# Revit family: Kessel 882505DN150 en
name_source: partatom
category: Pipe Accessories
revit_build: Autodesk Revit Architecture 2014 (Build: 20130308_1515(x64)
units: mm (PartAtom-declared; Revit-internal decimal feet)

## types (1)
- Kessel 882505DN150 en
    <1.010.00.2> Number of the part of the guideline = 38
    <1.010.00.3> Issue date (month) of the guideline = 201805
    <1.010.00.4> Manufacturer name = Kessel
    <1.010.00.5> Revision date of the file = 20190228
    <1.800.00.3> BS number = 100013000000000000000000000003000000???00000000008???00000
    <1.800.00.4> Comment field = Backwater chamber CO 1000 inlet DN 150, outlet DN 150, 2680 mm
    <1.810.00.3> Manufacturer’s reference number = 882505-DN150
    <1.810.00.4> DATANORM number = 882505-DN150
    <1.810.00.6> GTIN number = 4026092071304
    <1.960/3L.00.8> Link (URL) = http://www.kessel.de
    <38.100.00.4> Drain type for floor, roof and sanitary objects = Backwater valves
    <38.110.00.4> Floor, roof and sanitary works sequences = Backwater chamber CO 1000
    <38.400.00.3> Material of the drain body = polymer
    <38.700.00.15> Connection to GLT, GA = no
    <38.700.00.16> Fire resistance class can be retrofitted = no
    <38.700.00.4> product name = Backwater chamber CO 1000 inlet DN 150, outlet DN 150, 2680 mm
    <38.700.00.6> Complete article (one-piece) from combination (multi-part design) Drain body and attachment piece = yes
    <38.700.00.7> Potential compensation (ground connection) available = no
    <38.700.00.8> Electrical connection = no
    <38.710.13.3> Product name = Backwater chamber CO 1000 inlet DN 150, outlet DN 150, 2680 mm
    <38.710.13.4> Variant of the drainage drain = point drain
    <38.710.13.7> Leafy / Kiefang = no
    <38.710.15.3> Product name = Temporary protective cover
    <38.710.15.5> Material of the drain grate = plastic
    <38.710.15.9> Slip resistance of the drain grate = no
    <38.710.16.3> Type of measurements = external dimensions
    <38.710.16.7> Mass (net) = 130.5
    CONNECTOR0_DIAMETER_dX_0r = 0 mm  [stored 0 ft]
    CONNECTOR0_dX_00 = 515 mm
    CONNECTOR0_dX_01 = 505 mm
    CONNECTOR0_ref_dX = 505 mm
    CONNECTOR1_DIAMETER_dNBN0_0r = 0 mm  [stored 0 ft]
    CONNECTOR1_dNBN0_00 = 602 mm
    CONNECTOR1_dNBN0_01 = 592 mm
    CONNECTOR1_ref_dNBN0 = 592 mm
    CONNECTOR1_ref_dNBN1 = 228 mm
    CONNECTOR2_DIAMETER_dNBN0_0r = 0 mm  [stored 0 ft]
    CONNECTOR2_dNBN0_00 = 592 mm
    CONNECTOR2_dNBN0_01 = 602 mm
    CONNECTOR2_ref_dNBN0 = 592 mm
    CONNECTOR2_ref_dNBN1 = 228 mm
    CONNECTOR3_DIAMETER_dX_0r = 0 mm  [stored 0 ft]
    CONNECTOR3_dX_00 = 465 mm
    CONNECTOR3_dX_01 = 515 mm
    CONNECTOR3_ref_dNBN0 = 329 mm
    CONNECTOR3_ref_dNBN1 = 329 mm
    Manufacturer = Kessel
    Model = 882505-DN150
    URL = www.kessel.com

note: [stored X ft] marks values corroborated as IEEE doubles in the binary element streams (Revit-internal decimal feet)
